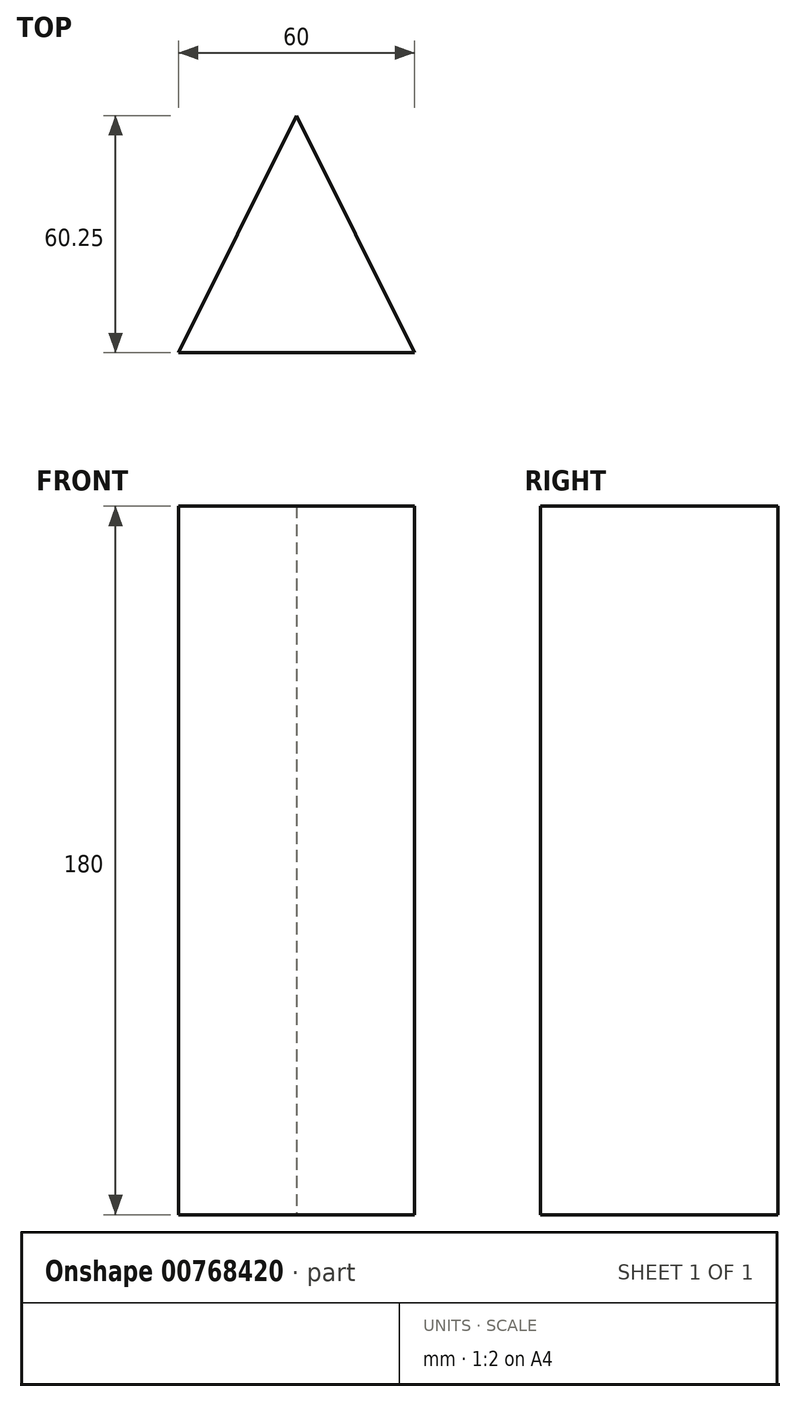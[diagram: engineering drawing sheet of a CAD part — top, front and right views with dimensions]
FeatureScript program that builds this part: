
annotation { "Feature Type Name" : "Feature", "Feature Type Description" : "" }
export const myFeature = defineFeature(function(context is Context, id is Id, definition is map)
    precondition{}
    {
        {
            var Q0;
            Q0=qCreatedBy(makeId("Top.planeOp"),FACE);
            var sketch = newSketch(context, id + "F0", { "sketchPlane" : qUnion([Q0])});
            skLineSegment(sketch, "E0", {"start": v(0, 0) * mm, "end": v(-60, 0) * mm});
            skLineSegment(sketch, "E1", {"start": v(-60, 0) * mm, "end": v(-30, 60.25) * mm});
            skLineSegment(sketch, "E2", {"start": v(-30, 60.25) * mm, "end": v(0, 0) * mm});
            skSolve(sketch);
        }
        {
            var Q0;
            Q0=makeQuery(id+"F0.imprint","IMPRINT",FACE,{"disambiguationData":[TD([[makeQuery(id+"F0.imprint","IMPRINT",EDGE,{"derivedFrom":sQuery(id+"F0.wireOp",EDGE,"E0")}),-1.0]])]});
            extrude(context, id + "F1", {"entities" : qUnion([Q0]), "depth" : 180 * mm, "offsetDistance" : 25 * mm});
        }
    });
